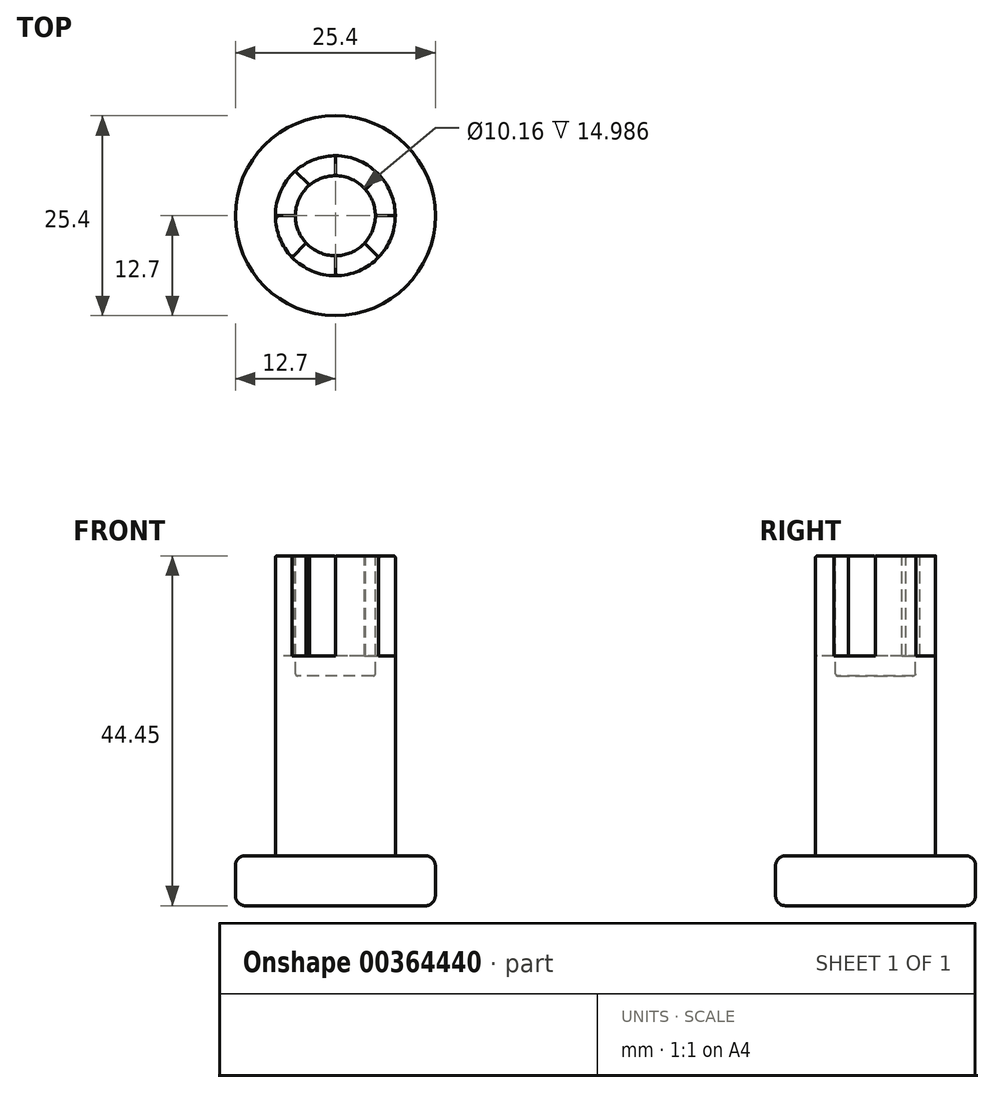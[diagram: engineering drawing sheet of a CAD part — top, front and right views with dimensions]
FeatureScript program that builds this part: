
annotation { "Feature Type Name" : "Feature", "Feature Type Description" : "" }
export const myFeature = defineFeature(function(context is Context, id is Id, definition is map)
    precondition{}
    {
        {
            var Q0;
            Q0=qCreatedBy(makeId("Top.planeOp"),FACE);
            var sketch = newSketch(context, id + "F0", { "sketchPlane" : qUnion([Q0])});
            skCircle(sketch, "E0", {"center": v(0, 0) * mm, "radius": 12.7 * mm});
            skSolve(sketch);
        }
        {
            var Q0;
            Q0=makeQuery(id+"F0.imprint","IMPRINT",FACE,{"disambiguationData":[TD([[makeQuery(id+"F0.imprint","IMPRINT",EDGE,{"derivedFrom":sQuery(id+"F0.wireOp",EDGE,"E0")}),1.0]])]});
            extrude(context, id + "F1", {"entities" : qUnion([Q0]), "depth" : 6.35 * mm});
        }
        {
            var Q0;
            Q0=makeQuery(id+"F1.opExtrude","CAP_EDGE",EDGE,{"disambiguationData":[OSD([sQuery(id+"F0.wireOp",EDGE,"E0")])],"isStart":false});
            var Q1;
            Q1=makeQuery(id+"F1.opExtrude","CAP_EDGE",EDGE,{"disambiguationData":[OSD([sQuery(id+"F0.wireOp",EDGE,"E0")])],"isStart":true});
            fillet(context, id + "F2", {"entities" : qUnion([Q0, Q1]), "radius" : 1.27 * mm, "tangentPropagation" : true, "allowEdgeOverflow" : false});
        }
        {
            var Q0;
            Q0=makeQuery(id+"F1.opExtrude","CAP_FACE",FACE,{"disambiguationData":[OSD([sQuery(id+"F0.wireOp",EDGE,"E0")])],"isStart":false});
            var sketch = newSketch(context, id + "F3", { "sketchPlane" : qUnion([Q0])});
            skCircle(sketch, "E1", {"center": v(0, 0) * mm, "radius": 7.62 * mm});
            skSolve(sketch);
        }
        {
            var Q0;
            Q0=makeQuery(id+"F3.imprint","IMPRINT",FACE,{"disambiguationData":[TD([[makeQuery(id+"F3.imprint","IMPRINT",EDGE,{"derivedFrom":sQuery(id+"F3.wireOp",EDGE,"E1")}),1.0]])]});
            extrude(context, id + "F4", {"entities" : qUnion([Q0]), "operationType" : NewBodyOperationType.ADD, "depth" : 38.1 * mm});
        }
        {
            var Q0;
            Q0=makeQuery(id+"F4.opExtrude","CAP_FACE",FACE,{"disambiguationData":[OSD([sQuery(id+"F3.wireOp",EDGE,"E1")])],"isStart":false});
            var sketch = newSketch(context, id + "F5", { "sketchPlane" : qUnion([Q0])});
            skCircle(sketch, "E2", {"center": v(0, 0) * mm, "radius": 5.08 * mm});
            skSolve(sketch);
        }
        {
            var Q0;
            Q0 = qSketchRegion(id + "F5", true);
            extrude(context, id + "F6", {"entities" : qUnion([Q0]), "operationType" : NewBodyOperationType.REMOVE, "oppositeDirection" : true, "depth" : 15.24 * mm});
        }
        {
            var Q0;
            Q0=makeQuery(id+"F4.opExtrude","CAP_FACE",FACE,{"disambiguationData":[OSD([sQuery(id+"F3.wireOp",EDGE,"E1")])],"isStart":false});
            var sketch = newSketch(context, id + "F7", { "sketchPlane" : qUnion([Q0])});
            skLineSegment(sketch, "E3", {"start": v(0, 5.08) * mm, "end": v(0, 7.62) * mm});
            skLineSegment(sketch, "E4", {"start": v(0, -5.08) * mm, "end": v(0, -7.62) * mm});
            skLineSegment(sketch, "E5", {"start": v(5.08, 0) * mm, "end": v(7.62, 0) * mm});
            skLineSegment(sketch, "E6", {"start": v(-5.08, 0) * mm, "end": v(-7.62, 0) * mm});
            skLineSegment(sketch, "E7", {"start": v(-3.3, 3.87) * mm, "end": v(-5.1, 5.67) * mm});
            skLineSegment(sketch, "E8", {"start": v(3.83, 3.34) * mm, "end": v(5.63, 5.14) * mm});
            skLineSegment(sketch, "E9", {"start": v(-3.7, -3.48) * mm, "end": v(-5.5, -5.28) * mm});
            skLineSegment(sketch, "E10", {"start": v(3.72, -3.46) * mm, "end": v(5.52, -5.26) * mm});
            skSolve(sketch);
        }
        {
            var Q0;
            {var subQ0=sQuery(id+"F7.wireOp",EDGE,"E5");Q0=makeQuery(id+"F7.imprint","IMPRINT",FACE,{"disambiguationData":[TD([[makeQuery(id+"F7.imprint","IMPRINT",EDGE,{"derivedFrom":subQ0}),-1.0]])]});}
            var Q1;
            {var subQ0=sQuery(id+"F7.wireOp",EDGE,"E4");Q1=makeQuery(id+"F7.imprint","IMPRINT",FACE,{"disambiguationData":[TD([[makeQuery(id+"F7.imprint","IMPRINT",EDGE,{"derivedFrom":subQ0}),-1.0]])]});}
            var Q2;
            {var subQ0=sQuery(id+"F7.wireOp",EDGE,"E6");Q2=makeQuery(id+"F7.imprint","IMPRINT",FACE,{"disambiguationData":[TD([[makeQuery(id+"F7.imprint","IMPRINT",EDGE,{"derivedFrom":subQ0}),-1.0]])]});}
            var Q3;
            {var subQ0=sQuery(id+"F7.wireOp",EDGE,"E3");Q3=makeQuery(id+"F7.imprint","IMPRINT",FACE,{"disambiguationData":[TD([[makeQuery(id+"F7.imprint","IMPRINT",EDGE,{"derivedFrom":subQ0}),-1.0]])]});}
            extrude(context, id + "F8", {"entities" : qUnion([Q0, Q1, Q2, Q3]), "operationType" : NewBodyOperationType.REMOVE, "oppositeDirection" : true, "depth" : 12.7 * mm});
        }
        {
            var Q0;
            Q0=makeQuery(id+"F8.boolean.opBoolean","COPY",EDGE,{"derivedFrom":makeQuery(id+"F8.opExtrude","SWEPT_EDGE",EDGE,{"disambiguationData":[OSD([sQuery(id+"F3.wireOp",EDGE,"E1"),sQuery(id+"F7.wireOp",EDGE,"E10")])]})});
            var Q1;
            Q1=makeQuery(id+"F8.boolean.opBoolean","COPY",EDGE,{"derivedFrom":makeQuery(id+"F8.opExtrude","SWEPT_EDGE",EDGE,{"disambiguationData":[OSD([sQuery(id+"F5.wireOp",EDGE,"E2"),sQuery(id+"F7.wireOp",EDGE,"E10")])]})});
            var Q2;
            {var subQ0=sQuery(id+"F5.wireOp",EDGE,"E2");var subQ1=makeQuery(id+"F6.boolean.opBoolean","COPY",EDGE,{"derivedFrom":makeQuery(id+"F6.opExtrude","CAP_EDGE",EDGE,{"disambiguationData":[OSD([subQ0])],"isStart":true})});Q2=makeQuery(id+"F8.boolean.opBoolean","COPY",EDGE,{"derivedFrom":makeQuery(id+"F8.opExtrude","CAP_EDGE",EDGE,{"disambiguationData":[OSD([subQ0]),TDD([makeQuery(id+"F7.imprint","IMPRINT",EDGE,{"disambiguationData":[TD([[makeQuery(id+"F7.imprint","INTERSECT",VERTEX,{"derivedFrom":[subQ1,sQuery(id+"F7.wireOp",EDGE,"E5")]}),1.0]])],"derivedFrom":subQ1})])],"isStart":false})});}
            var Q3;
            {var subQ0=sQuery(id+"F3.wireOp",EDGE,"E1");var subQ1=makeQuery(id+"F4.opExtrude","CAP_EDGE",EDGE,{"disambiguationData":[OSD([subQ0])],"isStart":false});Q3=makeQuery(id+"F8.boolean.opBoolean","COPY",EDGE,{"derivedFrom":makeQuery(id+"F8.opExtrude","CAP_EDGE",EDGE,{"disambiguationData":[OSD([subQ0]),TDD([makeQuery(id+"F7.imprint","IMPRINT",EDGE,{"disambiguationData":[TD([[makeQuery(id+"F7.imprint","INTERSECT",VERTEX,{"derivedFrom":[subQ1,sQuery(id+"F7.wireOp",EDGE,"E5")]}),1.0]])],"derivedFrom":subQ1})])],"isStart":false})});}
            var Q4;
            Q4=makeQuery(id+"F8.boolean.opBoolean","COPY",EDGE,{"derivedFrom":makeQuery(id+"F8.opExtrude","SWEPT_EDGE",EDGE,{"disambiguationData":[OSD([sQuery(id+"F3.wireOp",EDGE,"E1"),sQuery(id+"F7.wireOp",EDGE,"E5")])]})});
            var Q5;
            Q5=makeQuery(id+"F8.boolean.opBoolean","COPY",EDGE,{"derivedFrom":makeQuery(id+"F8.opExtrude","SWEPT_EDGE",EDGE,{"disambiguationData":[OSD([sQuery(id+"F3.wireOp",EDGE,"E1"),sQuery(id+"F7.wireOp",EDGE,"E8")])]})});
            var Q6;
            {var subQ0=sQuery(id+"F3.wireOp",EDGE,"E1");var subQ1=makeQuery(id+"F4.opExtrude","CAP_EDGE",EDGE,{"disambiguationData":[OSD([subQ0])],"isStart":false});Q6=makeQuery(id+"F8.boolean.opBoolean","COPY",EDGE,{"derivedFrom":makeQuery(id+"F8.opExtrude","CAP_EDGE",EDGE,{"disambiguationData":[OSD([subQ0]),TDD([makeQuery(id+"F7.imprint","IMPRINT",EDGE,{"disambiguationData":[TD([[makeQuery(id+"F7.imprint","INTERSECT",VERTEX,{"derivedFrom":[subQ1,sQuery(id+"F7.wireOp",EDGE,"E3")]}),1.0]])],"derivedFrom":subQ1})])],"isStart":false})});}
            var Q7;
            {var subQ0=sQuery(id+"F5.wireOp",EDGE,"E2");var subQ1=makeQuery(id+"F6.boolean.opBoolean","COPY",EDGE,{"derivedFrom":makeQuery(id+"F6.opExtrude","CAP_EDGE",EDGE,{"disambiguationData":[OSD([subQ0])],"isStart":true})});Q7=makeQuery(id+"F8.boolean.opBoolean","COPY",EDGE,{"derivedFrom":makeQuery(id+"F8.opExtrude","CAP_EDGE",EDGE,{"disambiguationData":[OSD([subQ0]),TDD([makeQuery(id+"F7.imprint","IMPRINT",EDGE,{"disambiguationData":[TD([[makeQuery(id+"F7.imprint","INTERSECT",VERTEX,{"derivedFrom":[subQ1,sQuery(id+"F7.wireOp",EDGE,"E3")]}),1.0]])],"derivedFrom":subQ1})])],"isStart":false})});}
            var Q8;
            Q8=makeQuery(id+"F8.boolean.opBoolean","COPY",EDGE,{"derivedFrom":makeQuery(id+"F8.opExtrude","SWEPT_EDGE",EDGE,{"disambiguationData":[OSD([sQuery(id+"F5.wireOp",EDGE,"E2"),sQuery(id+"F7.wireOp",EDGE,"E3")])]})});
            var Q9;
            Q9=makeQuery(id+"F8.boolean.opBoolean","COPY",EDGE,{"derivedFrom":makeQuery(id+"F8.opExtrude","SWEPT_EDGE",EDGE,{"disambiguationData":[OSD([sQuery(id+"F3.wireOp",EDGE,"E1"),sQuery(id+"F7.wireOp",EDGE,"E3")])]})});
            var Q10;
            Q10=makeQuery(id+"F8.boolean.opBoolean","COPY",EDGE,{"derivedFrom":makeQuery(id+"F8.opExtrude","SWEPT_EDGE",EDGE,{"disambiguationData":[OSD([sQuery(id+"F5.wireOp",EDGE,"E2"),sQuery(id+"F7.wireOp",EDGE,"E8")])]})});
            var Q11;
            Q11=makeQuery(id+"F8.boolean.opBoolean","COPY",EDGE,{"derivedFrom":makeQuery(id+"F8.opExtrude","SWEPT_EDGE",EDGE,{"disambiguationData":[OSD([sQuery(id+"F5.wireOp",EDGE,"E2"),sQuery(id+"F7.wireOp",EDGE,"E5")])]})});
            var Q12;
            {var subQ0=sQuery(id+"F3.wireOp",EDGE,"E1");Q12=makeQuery(id+"F8.boolean.opBoolean","SPLIT",EDGE,{"disambiguationData":[TD([makeQuery(id+"F8.opExtrude","SWEPT_FACE",FACE,{"disambiguationData":[OSD([sQuery(id+"F7.wireOp",EDGE,"E5")])]})])],"derivedFrom":makeQuery(id+"F4.opExtrude","CAP_EDGE",EDGE,{"disambiguationData":[OSD([subQ0])],"isStart":false})});}
            var Q13;
            {var subQ0=sQuery(id+"F5.wireOp",EDGE,"E2");Q13=makeQuery(id+"F8.boolean.opBoolean","SPLIT",EDGE,{"disambiguationData":[TD([makeQuery(id+"F8.opExtrude","SWEPT_FACE",FACE,{"disambiguationData":[OSD([sQuery(id+"F7.wireOp",EDGE,"E5")])]})])],"derivedFrom":makeQuery(id+"F6.boolean.opBoolean","COPY",EDGE,{"derivedFrom":makeQuery(id+"F6.opExtrude","CAP_EDGE",EDGE,{"disambiguationData":[OSD([subQ0])],"isStart":true})})});}
            var Q14;
            Q14=makeQuery(id+"F8.boolean.opBoolean","COPY",EDGE,{"derivedFrom":makeQuery(id+"F8.opExtrude","CAP_EDGE",EDGE,{"disambiguationData":[OSD([sQuery(id+"F7.wireOp",EDGE,"E5")])],"isStart":true})});
            var Q15;
            Q15=makeQuery(id+"F8.boolean.opBoolean","COPY",EDGE,{"derivedFrom":makeQuery(id+"F8.opExtrude","CAP_EDGE",EDGE,{"disambiguationData":[OSD([sQuery(id+"F7.wireOp",EDGE,"E8")])],"isStart":true})});
            var Q16;
            Q16=makeQuery(id+"F8.boolean.opBoolean","COPY",EDGE,{"derivedFrom":makeQuery(id+"F8.opExtrude","CAP_EDGE",EDGE,{"disambiguationData":[OSD([sQuery(id+"F7.wireOp",EDGE,"E10")])],"isStart":true})});
            var Q17;
            {var subQ0=sQuery(id+"F5.wireOp",EDGE,"E2");Q17=makeQuery(id+"F8.boolean.opBoolean","SPLIT",EDGE,{"disambiguationData":[TD([makeQuery(id+"F8.opExtrude","SWEPT_FACE",FACE,{"disambiguationData":[OSD([sQuery(id+"F7.wireOp",EDGE,"E4")])]})])],"derivedFrom":makeQuery(id+"F6.boolean.opBoolean","COPY",EDGE,{"derivedFrom":makeQuery(id+"F6.opExtrude","CAP_EDGE",EDGE,{"disambiguationData":[OSD([subQ0])],"isStart":true})})});}
            var Q18;
            {var subQ0=sQuery(id+"F3.wireOp",EDGE,"E1");Q18=makeQuery(id+"F8.boolean.opBoolean","SPLIT",EDGE,{"disambiguationData":[TD([makeQuery(id+"F8.opExtrude","SWEPT_FACE",FACE,{"disambiguationData":[OSD([sQuery(id+"F7.wireOp",EDGE,"E4")])]})])],"derivedFrom":makeQuery(id+"F4.opExtrude","CAP_EDGE",EDGE,{"disambiguationData":[OSD([subQ0])],"isStart":false})});}
            var Q19;
            Q19=makeQuery(id+"F8.boolean.opBoolean","COPY",EDGE,{"derivedFrom":makeQuery(id+"F8.opExtrude","CAP_EDGE",EDGE,{"disambiguationData":[OSD([sQuery(id+"F7.wireOp",EDGE,"E4")])],"isStart":true})});
            var Q20;
            Q20=makeQuery(id+"F8.boolean.opBoolean","COPY",EDGE,{"derivedFrom":makeQuery(id+"F8.opExtrude","SWEPT_EDGE",EDGE,{"disambiguationData":[OSD([sQuery(id+"F3.wireOp",EDGE,"E1"),sQuery(id+"F7.wireOp",EDGE,"E4")])]})});
            var Q21;
            {var subQ0=sQuery(id+"F3.wireOp",EDGE,"E1");Q21=makeQuery(id+"F8.boolean.opBoolean","SPLIT",EDGE,{"disambiguationData":[TD([makeQuery(id+"F8.opExtrude","SWEPT_FACE",FACE,{"disambiguationData":[OSD([sQuery(id+"F7.wireOp",EDGE,"E6")])]})])],"derivedFrom":makeQuery(id+"F4.opExtrude","CAP_EDGE",EDGE,{"disambiguationData":[OSD([subQ0])],"isStart":false})});}
            var Q22;
            {var subQ0=sQuery(id+"F5.wireOp",EDGE,"E2");Q22=makeQuery(id+"F8.boolean.opBoolean","SPLIT",EDGE,{"disambiguationData":[TD([makeQuery(id+"F8.opExtrude","SWEPT_FACE",FACE,{"disambiguationData":[OSD([sQuery(id+"F7.wireOp",EDGE,"E6")])]})])],"derivedFrom":makeQuery(id+"F6.boolean.opBoolean","COPY",EDGE,{"derivedFrom":makeQuery(id+"F6.opExtrude","CAP_EDGE",EDGE,{"disambiguationData":[OSD([subQ0])],"isStart":true})})});}
            var Q23;
            Q23=makeQuery(id+"F8.boolean.opBoolean","COPY",EDGE,{"derivedFrom":makeQuery(id+"F8.opExtrude","CAP_EDGE",EDGE,{"disambiguationData":[OSD([sQuery(id+"F7.wireOp",EDGE,"E9")])],"isStart":true})});
            var Q24;
            Q24=makeQuery(id+"F8.boolean.opBoolean","COPY",EDGE,{"derivedFrom":makeQuery(id+"F8.opExtrude","CAP_EDGE",EDGE,{"disambiguationData":[OSD([sQuery(id+"F7.wireOp",EDGE,"E6")])],"isStart":true})});
            var Q25;
            Q25=makeQuery(id+"F8.boolean.opBoolean","COPY",EDGE,{"derivedFrom":makeQuery(id+"F8.opExtrude","SWEPT_EDGE",EDGE,{"disambiguationData":[OSD([sQuery(id+"F3.wireOp",EDGE,"E1"),sQuery(id+"F7.wireOp",EDGE,"E9")])]})});
            var Q26;
            Q26=makeQuery(id+"F8.boolean.opBoolean","COPY",EDGE,{"derivedFrom":makeQuery(id+"F8.opExtrude","SWEPT_EDGE",EDGE,{"disambiguationData":[OSD([sQuery(id+"F5.wireOp",EDGE,"E2"),sQuery(id+"F7.wireOp",EDGE,"E4")])]})});
            var Q27;
            {var subQ0=sQuery(id+"F5.wireOp",EDGE,"E2");var subQ1=makeQuery(id+"F6.boolean.opBoolean","COPY",EDGE,{"derivedFrom":makeQuery(id+"F6.opExtrude","CAP_EDGE",EDGE,{"disambiguationData":[OSD([subQ0])],"isStart":true})});Q27=makeQuery(id+"F8.boolean.opBoolean","COPY",EDGE,{"derivedFrom":makeQuery(id+"F8.opExtrude","CAP_EDGE",EDGE,{"disambiguationData":[OSD([subQ0]),TDD([makeQuery(id+"F7.imprint","IMPRINT",EDGE,{"disambiguationData":[TD([[makeQuery(id+"F7.imprint","INTERSECT",VERTEX,{"derivedFrom":[subQ1,sQuery(id+"F7.wireOp",EDGE,"E4")]}),1.0]])],"derivedFrom":subQ1})])],"isStart":false})});}
            var Q28;
            {var subQ0=sQuery(id+"F3.wireOp",EDGE,"E1");var subQ1=makeQuery(id+"F4.opExtrude","CAP_EDGE",EDGE,{"disambiguationData":[OSD([subQ0])],"isStart":false});Q28=makeQuery(id+"F8.boolean.opBoolean","COPY",EDGE,{"derivedFrom":makeQuery(id+"F8.opExtrude","CAP_EDGE",EDGE,{"disambiguationData":[OSD([subQ0]),TDD([makeQuery(id+"F7.imprint","IMPRINT",EDGE,{"disambiguationData":[TD([[makeQuery(id+"F7.imprint","INTERSECT",VERTEX,{"derivedFrom":[subQ1,sQuery(id+"F7.wireOp",EDGE,"E4")]}),1.0]])],"derivedFrom":subQ1})])],"isStart":false})});}
            var Q29;
            {var subQ0=sQuery(id+"F3.wireOp",EDGE,"E1");var subQ1=makeQuery(id+"F4.opExtrude","CAP_EDGE",EDGE,{"disambiguationData":[OSD([subQ0])],"isStart":false});Q29=makeQuery(id+"F8.boolean.opBoolean","COPY",EDGE,{"derivedFrom":makeQuery(id+"F8.opExtrude","CAP_EDGE",EDGE,{"disambiguationData":[OSD([subQ0]),TDD([makeQuery(id+"F7.imprint","IMPRINT",EDGE,{"disambiguationData":[TD([[makeQuery(id+"F7.imprint","INTERSECT",VERTEX,{"derivedFrom":[subQ1,sQuery(id+"F7.wireOp",EDGE,"E6")]}),1.0]])],"derivedFrom":subQ1})])],"isStart":false})});}
            var Q30;
            {var subQ0=sQuery(id+"F5.wireOp",EDGE,"E2");var subQ1=makeQuery(id+"F6.boolean.opBoolean","COPY",EDGE,{"derivedFrom":makeQuery(id+"F6.opExtrude","CAP_EDGE",EDGE,{"disambiguationData":[OSD([subQ0])],"isStart":true})});Q30=makeQuery(id+"F8.boolean.opBoolean","COPY",EDGE,{"derivedFrom":makeQuery(id+"F8.opExtrude","CAP_EDGE",EDGE,{"disambiguationData":[OSD([subQ0]),TDD([makeQuery(id+"F7.imprint","IMPRINT",EDGE,{"disambiguationData":[TD([[makeQuery(id+"F7.imprint","INTERSECT",VERTEX,{"derivedFrom":[subQ1,sQuery(id+"F7.wireOp",EDGE,"E6")]}),1.0]])],"derivedFrom":subQ1})])],"isStart":false})});}
            var Q31;
            Q31=makeQuery(id+"F8.boolean.opBoolean","COPY",EDGE,{"derivedFrom":makeQuery(id+"F8.opExtrude","SWEPT_EDGE",EDGE,{"disambiguationData":[OSD([sQuery(id+"F5.wireOp",EDGE,"E2"),sQuery(id+"F7.wireOp",EDGE,"E7")])]})});
            var Q32;
            Q32=makeQuery(id+"F8.boolean.opBoolean","COPY",EDGE,{"derivedFrom":makeQuery(id+"F8.opExtrude","SWEPT_EDGE",EDGE,{"disambiguationData":[OSD([sQuery(id+"F3.wireOp",EDGE,"E1"),sQuery(id+"F7.wireOp",EDGE,"E7")])]})});
            var Q33;
            Q33=makeQuery(id+"F8.boolean.opBoolean","COPY",EDGE,{"derivedFrom":makeQuery(id+"F8.opExtrude","CAP_EDGE",EDGE,{"disambiguationData":[OSD([sQuery(id+"F7.wireOp",EDGE,"E7")])],"isStart":true})});
            var Q34;
            Q34=makeQuery(id+"F8.boolean.opBoolean","COPY",EDGE,{"derivedFrom":makeQuery(id+"F8.opExtrude","CAP_EDGE",EDGE,{"disambiguationData":[OSD([sQuery(id+"F7.wireOp",EDGE,"E3")])],"isStart":true})});
            var Q35;
            Q35=makeQuery(id+"F8.boolean.opBoolean","COPY",EDGE,{"derivedFrom":makeQuery(id+"F8.opExtrude","SWEPT_EDGE",EDGE,{"disambiguationData":[OSD([sQuery(id+"F3.wireOp",EDGE,"E1"),sQuery(id+"F7.wireOp",EDGE,"E6")])]})});
            var Q36;
            Q36=makeQuery(id+"F8.boolean.opBoolean","COPY",EDGE,{"derivedFrom":makeQuery(id+"F8.opExtrude","SWEPT_EDGE",EDGE,{"disambiguationData":[OSD([sQuery(id+"F5.wireOp",EDGE,"E2"),sQuery(id+"F7.wireOp",EDGE,"E6")])]})});
            var Q37;
            Q37=makeQuery(id+"F8.boolean.opBoolean","COPY",EDGE,{"derivedFrom":makeQuery(id+"F8.opExtrude","SWEPT_EDGE",EDGE,{"disambiguationData":[OSD([sQuery(id+"F5.wireOp",EDGE,"E2"),sQuery(id+"F7.wireOp",EDGE,"E9")])]})});
            fillet(context, id + "F9", {"entities" : qUnion([Q0, Q1, Q2, Q3, Q4, Q5, Q6, Q7, Q8, Q9, Q10, Q11, Q12, Q13, Q14, Q15, Q16, Q17, Q18, Q19, Q20, Q21, Q22, Q23, Q24, Q25, Q26, Q27, Q28, Q29, Q30, Q31, Q32, Q33, Q34, Q35, Q36, Q37]), "radius" : 0.25 * mm, "tangentPropagation" : true, "allowEdgeOverflow" : false});
        }
        {
            var Q0;
            Q0=makeQuery(id+"F4.opExtrude","CAP_EDGE",EDGE,{"disambiguationData":[OSD([sQuery(id+"F3.wireOp",EDGE,"E1")])],"isStart":true});
            var Q1;
            Q1=makeQuery(id+"F6.boolean.opBoolean","COPY",EDGE,{"derivedFrom":makeQuery(id+"F6.opExtrude","CAP_EDGE",EDGE,{"disambiguationData":[OSD([sQuery(id+"F5.wireOp",EDGE,"E2")])],"isStart":false})});
            fillet(context, id + "F10", {"entities" : qUnion([Q0, Q1]), "radius" : 0.25 * mm, "tangentPropagation" : true, "allowEdgeOverflow" : false});
        }
    });
